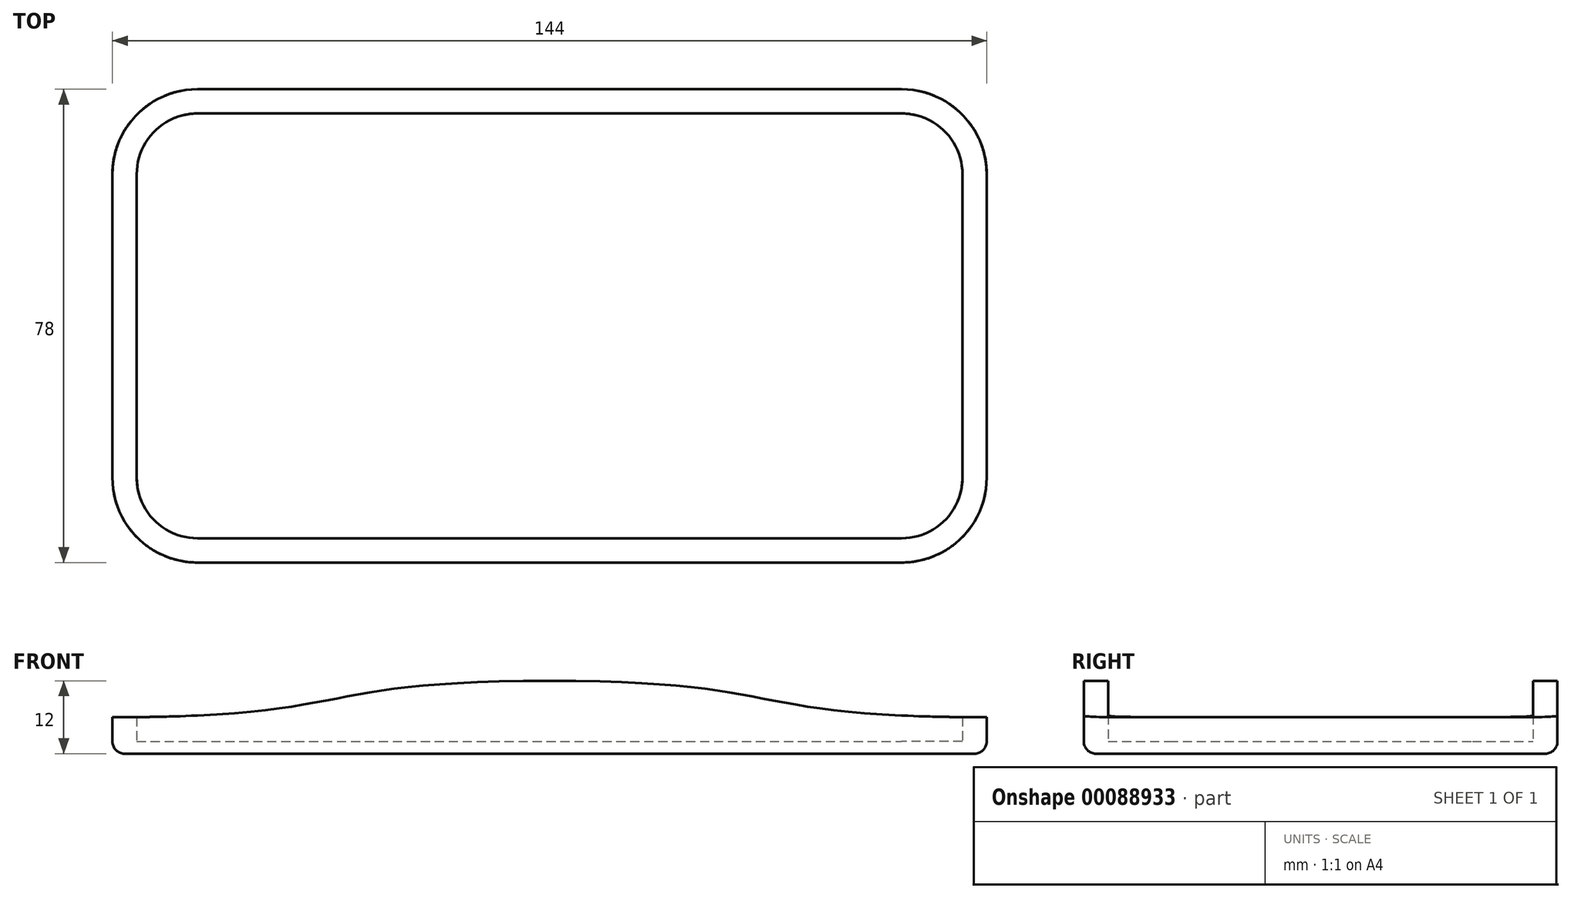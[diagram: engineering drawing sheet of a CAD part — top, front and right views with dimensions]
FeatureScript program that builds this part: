
annotation { "Feature Type Name" : "Feature", "Feature Type Description" : "" }
export const myFeature = defineFeature(function(context is Context, id is Id, definition is map)
    precondition{}
    {
        {
            var Q0;
            Q0=qCreatedBy(makeId("Top.planeOp"),FACE);
            var sketch = newSketch(context, id + "F0", { "sketchPlane" : qUnion([Q0])});
            skLineSegment(sketch, "E0.bottom", {"start": v(-58, -35) * mm, "end": v(58, -35) * mm});
            skLineSegment(sketch, "E0.top", {"start": v(-58, 35) * mm, "end": v(58, 35) * mm});
            skLineSegment(sketch, "E0.left", {"start": v(-68, -25) * mm, "end": v(-68, 25) * mm});
            skLineSegment(sketch, "E0.right", {"start": v(68, -25) * mm, "end": v(68, 25) * mm});
            skPoint(sketch, "E0.middle", {"position": v(0, 0) * mm});
            skPoint(sketch, "E1.visualSharp", {"position": v(-68, 35) * mm});
            skArc(sketch, "E1.filletArc", {"start": v(-58, 35) * mm, "mid": v(-65.07, 32.07) * mm, "end": v(-68, 25) * mm});
            skPoint(sketch, "E2.visualSharp", {"position": v(68, 35) * mm});
            skArc(sketch, "E2.filletArc", {"start": v(68, 25) * mm, "mid": v(65.07, 32.07) * mm, "end": v(58, 35) * mm});
            skPoint(sketch, "E3.visualSharp", {"position": v(68, -35) * mm});
            skArc(sketch, "E3.filletArc", {"start": v(58, -35) * mm, "mid": v(65.07, -32.07) * mm, "end": v(68, -25) * mm});
            skPoint(sketch, "E4.visualSharp", {"position": v(-68, -35) * mm});
            skArc(sketch, "E4.filletArc", {"start": v(-68, -25) * mm, "mid": v(-65.07, -32.07) * mm, "end": v(-58, -35) * mm});
            skArc(sketch, "E5.0", {"start": v(-58, 39) * mm, "mid": v(-67.9, 34.9) * mm, "end": v(-72, 25) * mm});
            skLineSegment(sketch, "E5.1", {"start": v(-72, -25) * mm, "end": v(-72, 25) * mm});
            skLineSegment(sketch, "E5.2", {"start": v(-58, 39) * mm, "end": v(58, 39) * mm});
            skArc(sketch, "E5.3", {"start": v(-72, -25) * mm, "mid": v(-67.9, -34.9) * mm, "end": v(-58, -39) * mm});
            skArc(sketch, "E5.4", {"start": v(72, 25) * mm, "mid": v(67.9, 34.9) * mm, "end": v(58, 39) * mm});
            skLineSegment(sketch, "E5.5", {"start": v(72, -25) * mm, "end": v(72, 25) * mm});
            skArc(sketch, "E5.6", {"start": v(58, -39) * mm, "mid": v(67.9, -34.9) * mm, "end": v(72, -25) * mm});
            skLineSegment(sketch, "E5.7", {"start": v(-58, -39) * mm, "end": v(58, -39) * mm});
            skSolve(sketch);
        }
        {
            var Q0;
            Q0=makeQuery(id+"F0.imprint","IMPRINT",FACE,{"disambiguationData":[TD([[makeQuery(id+"F0.imprint","IMPRINT",EDGE,{"derivedFrom":sQuery(id+"F0.wireOp",EDGE,"E0.bottom")}),1.0]])]});
            extrude(context, id + "F1", {"entities" : qUnion([Q0]), "depth" : 2 * mm});
        }
        {
            var Q0;
            Q0=makeQuery(id+"F0.imprint","IMPRINT",FACE,{"disambiguationData":[TD([[makeQuery(id+"F0.imprint","IMPRINT",EDGE,{"derivedFrom":sQuery(id+"F0.wireOp",EDGE,"E0.bottom")}),-1.0]])]});
            extrude(context, id + "F2", {"entities" : qUnion([Q0]), "operationType" : NewBodyOperationType.ADD, "depth" : 12 * mm});
        }
        {
            var Q0;
            Q0=qCreatedBy(makeId("Front.planeOp"),FACE);
            var sketch = newSketch(context, id + "F3", { "sketchPlane" : qUnion([Q0])});
            skLineSegment(sketch, "E6.0", {"start": v(-58, 12) * mm, "end": v(58, 12) * mm});
            skLineSegment(sketch, "E7.0", {"start": v(-72, 0) * mm, "end": v(72, 0) * mm});
            skLineSegment(sketch, "E8.0", {"start": v(-72, 12) * mm, "end": v(-72, 0) * mm});
            skLineSegment(sketch, "E9.0", {"start": v(72, 12) * mm, "end": v(72, 0) * mm});
            skFitSpline(sketch, "E10", {"points": [v(-72, 6) * mm, v(0, 12) * mm], "startDerivative": vector(124.49, 0) * mm, "endDerivative": vector(120.7, 0) * mm});
            skLineSegment(sketch, "E11", {"start": v(0, 12) * mm, "end": v(0, 0) * mm, "construction": true});
            skFitSpline(sketch, "E12.MirrorCS", {"points": [v(72, 6) * mm, v(0, 12) * mm], "startDerivative": vector(-124.49, 0) * mm, "endDerivative": vector(-120.7, 0) * mm});
            skPoint(sketch, "E13.orphan", {"position": v(-58, 0) * mm});
            skPoint(sketch, "E14.orphan", {"position": v(58, 0) * mm});
            skSolve(sketch);
        }
        {
            var Q0;
            {var subQ2=sQuery(id+"F3.wireOp",EDGE,"E7.0");Q0=makeQuery(id+"F3.imprint","IMPRINT",FACE,{"disambiguationData":[TD([[makeQuery(id+"F3.imprint","IMPRINT",EDGE,{"derivedFrom":subQ2}),1.0]])]});}
            extrude(context, id + "F4", {"entities" : qUnion([Q0]), "operationType" : NewBodyOperationType.INTERSECT, "endBound" : BoundingType.SYMMETRIC, "depth" : 99 * mm});
        }
        {
            var Q0;
            Q0=makeQuery(id+"F1.opExtrude","CAP_EDGE",EDGE,{"disambiguationData":[OSD([sQuery(id+"F0.wireOp",EDGE,"E4.filletArc")])],"isStart":false});
            var Q1;
            Q1=makeQuery(id+"F1.opExtrude","CAP_EDGE",EDGE,{"disambiguationData":[OSD([sQuery(id+"F0.wireOp",EDGE,"E3.filletArc")])],"isStart":false});
            var Q2;
            Q2=makeQuery(id+"F2.opExtrude","CAP_EDGE",EDGE,{"disambiguationData":[OSD([sQuery(id+"F0.wireOp",EDGE,"E5.3")])],"isStart":true});
            fillet(context, id + "F5", {"entities" : qUnion([Q0, Q1, Q2]), "radius" : 2 * mm, "tangentPropagation" : true, "allowEdgeOverflow" : false});
        }
    });
